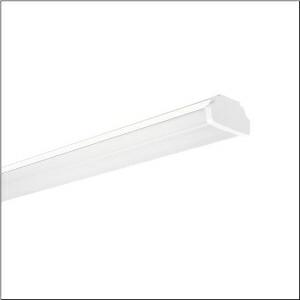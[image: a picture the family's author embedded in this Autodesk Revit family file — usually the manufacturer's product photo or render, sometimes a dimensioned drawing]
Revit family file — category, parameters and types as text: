
# Revit family: modario_31_gen_2_53bm812mv4fxd2_69c1
name_source: partatom
category: Lighting Fixtures
units: mm (PartAtom-declared; Revit-internal decimal feet)

## family parameters
Cut with Voids When Loaded = No
Host = Face
Light Source = No
Part Type = Normal
Room Calculation Point = No
Round Connector Dimension = Use Diameter
Shared = No

## types (1)
- --- (1 x LED, 15440 lm, 82.3 W, 4000K)
    Apparent Load = 82 VA
    CIE Flux Codes = 47 80 95 93 100
    Color Rendering = 80
    Color Temperature = 4000K
    Default Elevation = 1800 mm
    Description = Modario 31 Gen.2, luminaire insert, of sheet steel, coil coated, white, length: 1.495mm, width: 81mm, height: 82mm, 5x system unit, system units: 299mm, LED rated luminous flux: 15.440lm, light colour: 840, SDCM (Standard Deviation of Colour Matching)MacAdam ≤ 3 SDCM (initial), control gear: ON/OFF Multilumen, control gear: ECG, with plug, 3-pole, with phase selection, mains connection: 220..240V, AC, 50/60Hz, rated input power: 82W, through-wiring accessed according to module size, primary optical cover: cover, of PMMA, light emission: direct distribution, primary light characteristic: symmetric, protection rating (complete): IP20, protection rating (LED compartment): IP50, insulation class (complete): insulation class I (protective earthing), certification: CE, ENEC, VDE, UKCA, impact resistance: IK03, permissible ambient temperature for indoor applications: -35..+35°C, corresponds to IFS (International Featured Standards) requirements for safety and quality in the food industry, reducing of maximum allowable ambient temperature of 5°C with ceiling mounting, IP40 when using the optional accessory 5TP9018, packaging unit: 1 piece
    Height = 92 mm
    Lamp = 1 x LED
    Lamp Light Flux = 15440 lm
    Lamp Power = 82.3 W
    Lamp count = 1
    Length = 1495 mm
    Luminous efficacy = 188 lm/W
    Manufacturer = Siteco
    ModVariant = No
    Model = 53BM812MV4FXD2
    Mounting Place = Ceiling
    Mounting Type = Pendant
    Number of Poles = 1
    OnlyDefault = Yes
    Power Factor = 1
    Product Name = Modario 31 Gen.2
    Product group = luminaire insert | ceiling pendant
    ProductGroupID = 901
    Protection Class = Protection class I
    Protection Degree = IP 20
    RLX_Detail_Level = 1
    RLX_Emergency_Light_Flux = 0 lm
    RLX_Emergency_Type = 0
    RLX_Emergency_Type_DB = No
    RlxData = <blob elided: 40053 chars, md5=0b18238e>
    Socket = socket
    Standby Power = 0 W
    System Light Flux = 15440 lm
    System Power = 82 W
    Type Comments = factory setting: luminous flux: 100 % | (A | C | E) | 193 mA
    Type Image = l_1341886.jpg
    URL = http://relux.com
    VarID = @adj_050817
    Voltage = 0 V
    Weight = 0.00 kg
    Width = 81 mm

## geometry (parser evidence)
native form markers: Blend x4, Sweep x12
no freeform markers — native parametric forms only
